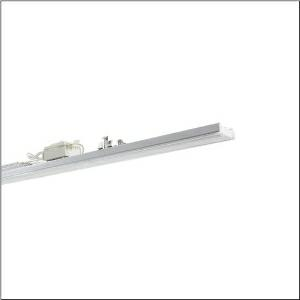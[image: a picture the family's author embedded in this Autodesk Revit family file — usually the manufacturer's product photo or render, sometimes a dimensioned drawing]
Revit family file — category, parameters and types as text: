
# Revit family: licross_r__11_recessed_mo_51tl12dv455g_7199
name_source: partatom
category: Lighting Fixtures
units: mm (PartAtom-declared; Revit-internal decimal feet)

## family parameters
Cut with Voids When Loaded = No
Host = Face
Light Source = No
Part Type = Normal
Room Calculation Point = No
Round Connector Dimension = Use Diameter
Shared = No

## types (1)
- --- (1 x LED, 5700 lm, 29.1 W, 4000K)
    Apparent Load = 29 VA
    CIE Flux Codes = 67 92 99 100 100
    Color Rendering = 80
    Color Temperature = 4000K
    Default Elevation = 1800 mm
    Description = Licross® 11 Recessed MO, luminaire insert, of sheet steel, coil coated, white, length: 2.250mm, width: 66mm, height: 67mm, LED rated luminous flux: 5.700lm, light colour: 840, control gear: DALI 2, with plug, 5-pole, with phase selection, mains connection: 220..240V, AC, 50/60Hz, rated input power: 29W, internal wiring halogen-free, primary optical cover: cover, of PMMA, light emission: direct distribution, primary light characteristic: symmetric, protection rating (complete): IP40, insulation class (complete): insulation class I (protective earthing), certification: CE, ENEC, VDE, UKCA, protection symbol: D if used in an environment without relevant dust loads with corresponding accessories, impact resistance: IK06, permissible ambient temperature for indoor applications: -25..+45°C, corresponds to IFS (International Featured Standards) requirements for safety and quality in the food industry, reducing of maximum allowable ambient temperature of 5°C with ceiling mounting, LABS conformity tested according to VDMA 24364:2018-05, packaging unit: 1 piece
    Height = 58 mm
    Lamp = 1 x LED
    Lamp Light Flux = 5700 lm
    Lamp Power = 29.1 W
    Lamp count = 1
    Length = 2250 mm
    Luminous efficacy = 196 lm/W
    Manufacturer = Siteco
    ModVariant = No
    Model = 51TL12DV455G
    Mounting Place = Ceiling
    Mounting Type = Pendant
    Number of Poles = 1
    OnlyDefault = Yes
    Power Factor = 1
    Product Name = Licross® 11 Recessed MO
    Product group = luminaire insert | ceiling pendant
    ProductGroupID = 902
    Protection Class = Protection class I
    Protection Degree = IP 40
    RLX_Detail_Level = 1
    RLX_Emergency_Light_Flux = 0 lm
    RLX_Emergency_Type = 0
    RLX_Emergency_Type_DB = No
    RlxData = <blob elided: 29245 chars, md5=2b4c5e38>
    Socket = socket
    Standby Power = 0 W
    System Light Flux = 5700 lm
    System Power = 29 W
    Type Comments = factory setting: luminous flux: 100 % | dim-lin: 254 | 133 mA
    Type Image = l_1296930.jpg
    URL = http://relux.com
    VarID = @adj_121783
    Voltage = 0 V
    Weight = 0.00 kg
    Width = 66 mm

## geometry (parser evidence)
native form markers: Blend x4, Sweep x11
no freeform markers — native parametric forms only
